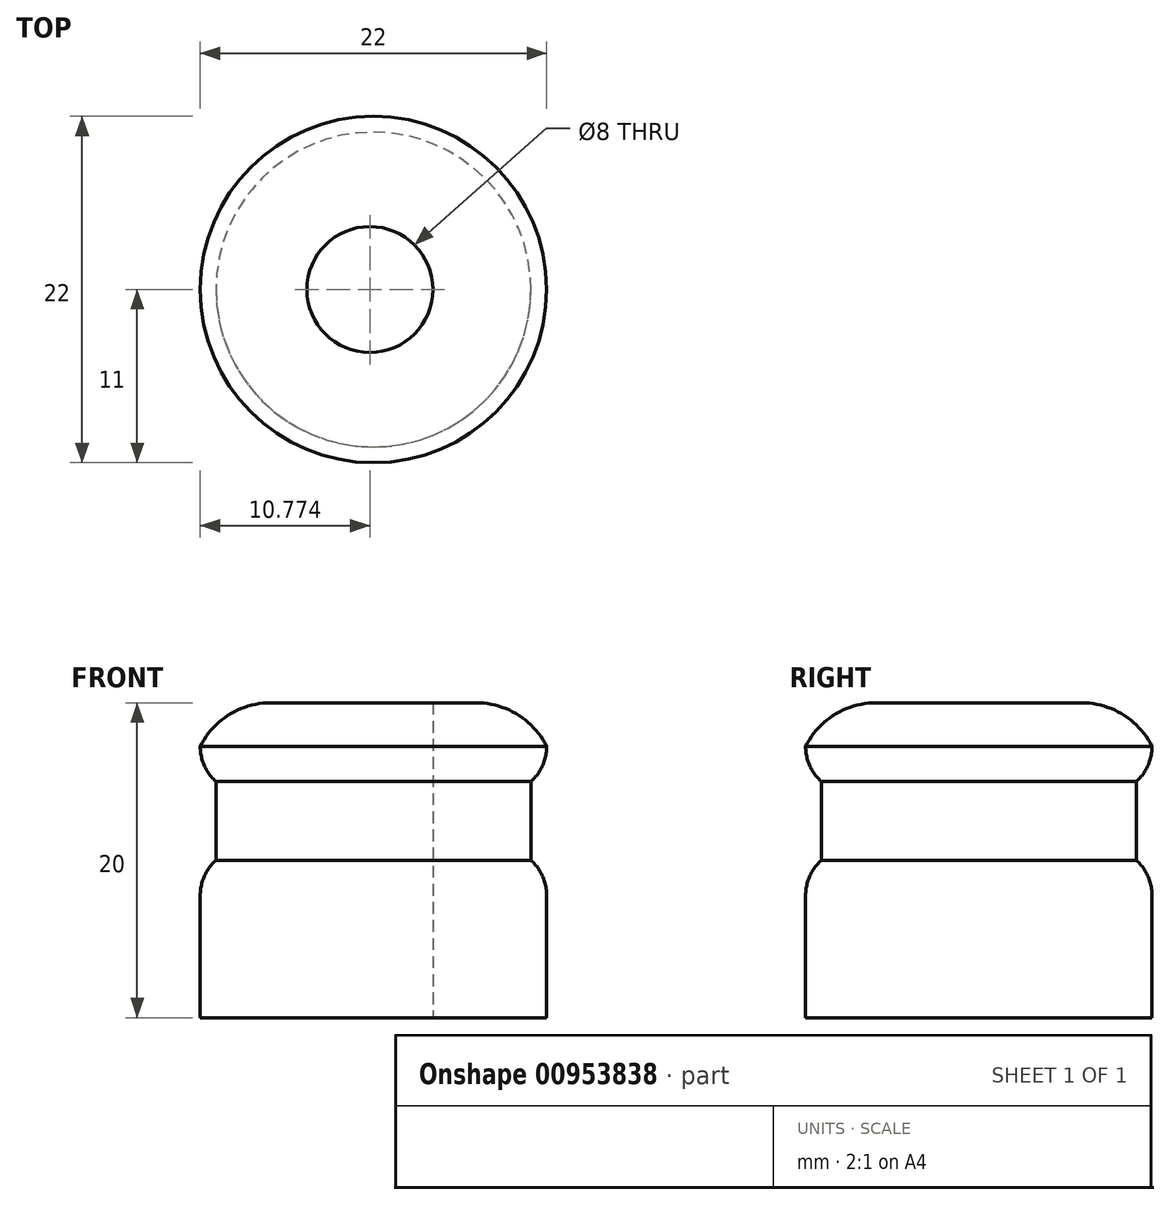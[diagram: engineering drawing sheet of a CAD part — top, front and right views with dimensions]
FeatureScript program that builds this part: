
annotation { "Feature Type Name" : "Feature", "Feature Type Description" : "" }
export const myFeature = defineFeature(function(context is Context, id is Id, definition is map)
    precondition{}
    {
        {
            var Q0;
            Q0=qCreatedBy(makeId("Top.planeOp"),FACE);
            var sketch = newSketch(context, id + "F0", { "sketchPlane" : qUnion([Q0])});
            skCircle(sketch, "E0", {"center": v(0, 0) * mm, "radius": 11 * mm});
            skCircle(sketch, "E1", {"center": v(-0.23, 0) * mm, "radius": 4 * mm});
            skSolve(sketch);
        }
        {
            var Q0;
            Q0=makeQuery(id+"F0.imprint","IMPRINT",FACE,{"disambiguationData":[TD([[makeQuery(id+"F0.imprint","IMPRINT",EDGE,{"derivedFrom":sQuery(id+"F0.wireOp",EDGE,"E0")}),1.0]])]});
            extrude(context, id + "F1", {"entities" : qUnion([Q0]), "depth" : 10 * mm, "offsetDistance" : 25 * mm});
        }
        {
            var Q0;
            Q0=makeQuery(id+"F1.opExtrude","CAP_FACE",FACE,{"disambiguationData":[OSD([sQuery(id+"F0.wireOp",EDGE,"E0")])],"isStart":false});
            var sketch = newSketch(context, id + "F2", { "sketchPlane" : qUnion([Q0])});
            skCircle(sketch, "E2", {"center": v(0, 0) * mm, "radius": 10 * mm});
            skSolve(sketch);
        }
        {
            var Q0;
            Q0=makeQuery(id+"F2.imprint","IMPRINT",FACE,{"disambiguationData":[TD([[makeQuery(id+"F2.imprint","IMPRINT",EDGE,{"derivedFrom":sQuery(id+"F2.wireOp",EDGE,"E2")}),1.0]])]});
            extrude(context, id + "F3", {"entities" : qUnion([Q0]), "operationType" : NewBodyOperationType.ADD, "depth" : 5 * mm, "offsetDistance" : 25 * mm});
        }
        {
            var Q0;
            Q0=makeQuery(id+"F3.opExtrude","CAP_FACE",FACE,{"disambiguationData":[OSD([sQuery(id+"F2.wireOp",EDGE,"E2")])],"isStart":false});
            var sketch = newSketch(context, id + "F4", { "sketchPlane" : qUnion([Q0])});
            skCircle(sketch, "E3", {"center": v(0, 0) * mm, "radius": 11 * mm});
            skSolve(sketch);
        }
        {
            var Q0;
            Q0=makeQuery(id+"F4.imprint","IMPRINT",FACE,{"disambiguationData":[TD([[makeQuery(id+"F4.imprint","IMPRINT",EDGE,{"derivedFrom":sQuery(id+"F4.wireOp",EDGE,"E3")}),1.0]])]});
            var Q1;
            Q1=makeQuery(id+"F4.imprint","IMPRINT",FACE,{"disambiguationData":[TD([[makeQuery(id+"F4.imprint","IMPRINT",EDGE,{"derivedFrom":makeQuery(id+"F3.opExtrude","CAP_EDGE",EDGE,{"disambiguationData":[OSD([sQuery(id+"F2.wireOp",EDGE,"E2")])],"isStart":false})}),1.0]])]});
            extrude(context, id + "F5", {"entities" : qUnion([Q0, Q1]), "operationType" : NewBodyOperationType.ADD, "depth" : 5 * mm, "offsetDistance" : 25 * mm});
        }
        {
            var Q0;
            Q0=makeQuery(id+"F5.opExtrude","CAP_EDGE",EDGE,{"disambiguationData":[OSD([sQuery(id+"F4.wireOp",EDGE,"E3")])],"isStart":true});
            var Q1;
            Q1=makeQuery(id+"F1.opExtrude","CAP_EDGE",EDGE,{"disambiguationData":[OSD([sQuery(id+"F0.wireOp",EDGE,"E0")])],"isStart":false});
            fillet(context, id + "F6", {"entities" : qUnion([Q0, Q1]), "radius" : 3 * mm, "tangentPropagation" : true, "allowEdgeOverflow" : false});
        }
        {
            var Q0;
            Q0=makeQuery(id+"F5.opExtrude","CAP_EDGE",EDGE,{"disambiguationData":[OSD([sQuery(id+"F4.wireOp",EDGE,"E3")])],"isStart":false});
            fillet(context, id + "F7", {"entities" : qUnion([Q0]), "radius" : 5 * mm, "tangentPropagation" : true, "allowEdgeOverflow" : false});
        }
    });
